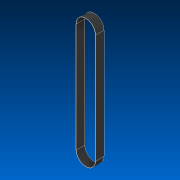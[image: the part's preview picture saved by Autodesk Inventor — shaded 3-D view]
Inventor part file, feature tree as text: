
AUTODESK INVENTOR PART (.ipt)
format: ipt  version: 2022 (Build 260153000, 153)  size: 93,184 bytes
history: native  units: in
note: dims shown in document units (in); Inventor stores cm internally (conversion verified against a paired STEP export)
features: extrude x1, sketch x1
ambient origin geometry x8: Origin, YZ Plane, XZ Plane, XY Plane, X Axis, Y Axis, Z Axis, Center Point
bodies: Solid1 (feature_tree)
feature tree (2):
  extrude  "Extrusion1"  Depth=0.0625in
  sketch  "Sketch1"  dims[d0=19.5in d2=0.0625in d3=1.5in d4=0.0in d5=3.5in]
